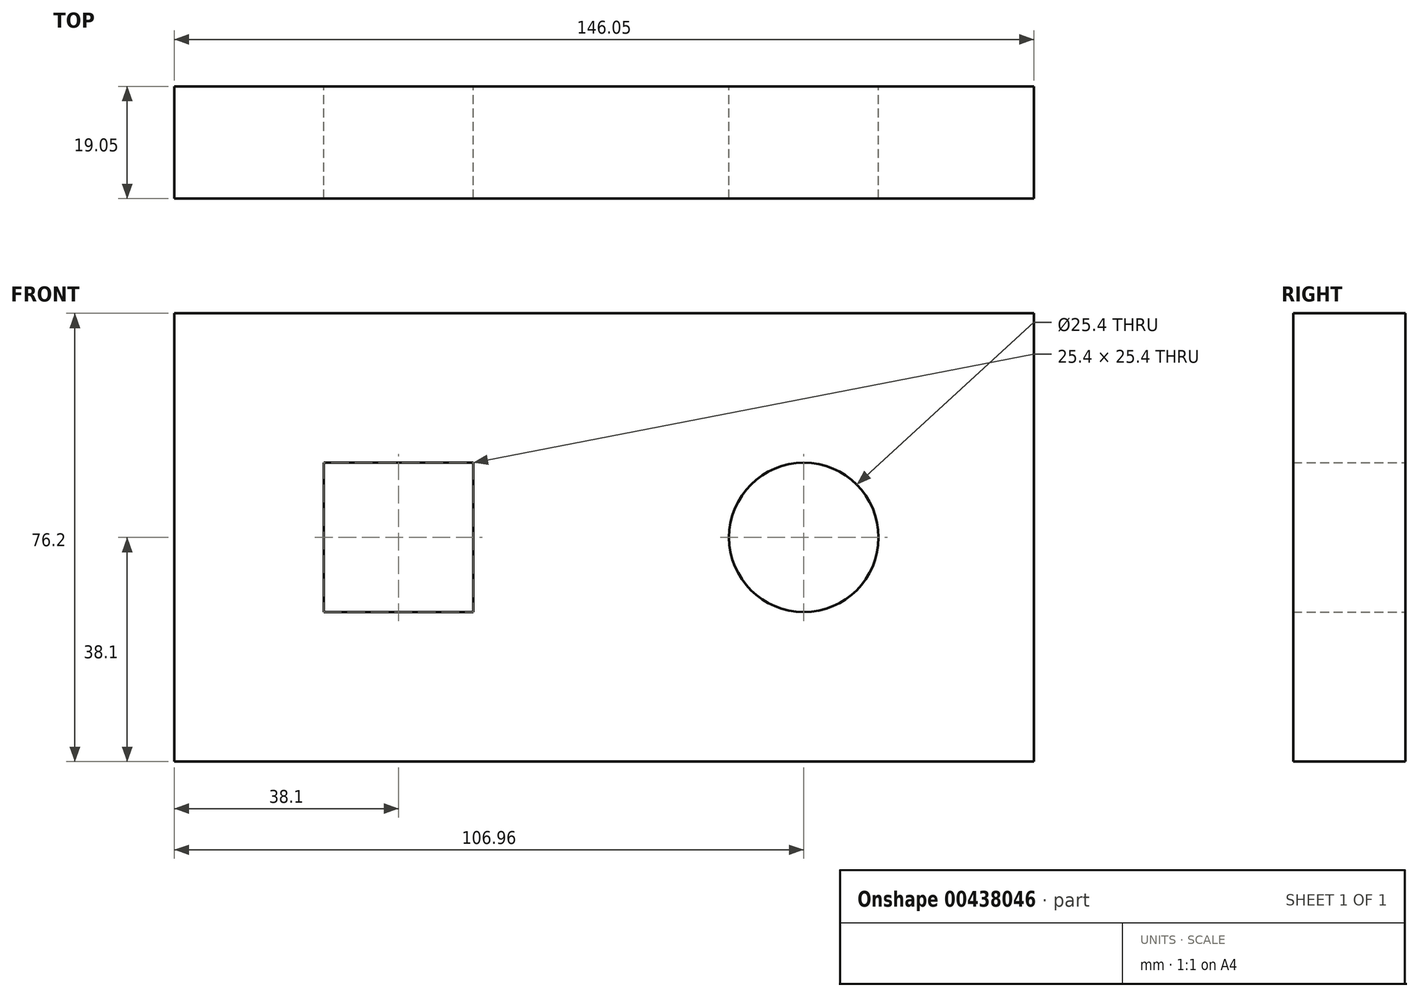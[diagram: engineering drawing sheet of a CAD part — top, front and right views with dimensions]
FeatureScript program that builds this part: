
annotation { "Feature Type Name" : "Feature", "Feature Type Description" : "" }
export const myFeature = defineFeature(function(context is Context, id is Id, definition is map)
    precondition{}
    {
        {
            var Q0;
            Q0=qCreatedBy(makeId("Front.planeOp"),FACE);
            var sketch = newSketch(context, id + "F0", { "sketchPlane" : qUnion([Q0])});
            skLineSegment(sketch, "E0", {"start": v(0, 0) * mm, "end": v(-146.05, 0) * mm});
            skLineSegment(sketch, "E1", {"start": v(-146.05, 0) * mm, "end": v(-146.05, 76.2) * mm});
            skLineSegment(sketch, "E2", {"start": v(-146.05, 76.2) * mm, "end": v(0, 76.2) * mm});
            skLineSegment(sketch, "E3", {"start": v(0, 76.2) * mm, "end": v(0, 0) * mm});
            skCircle(sketch, "E4", {"center": v(-39.1, 38.1) * mm, "radius": 12.7 * mm});
            skPoint(sketch, "E4.centerSnap0", {"position": v(0, 38.1) * mm});
            skLineSegment(sketch, "E5.bottom", {"start": v(-120.65, 50.8) * mm, "end": v(-95.25, 50.8) * mm});
            skLineSegment(sketch, "E5.top", {"start": v(-120.65, 25.4) * mm, "end": v(-95.25, 25.4) * mm});
            skLineSegment(sketch, "E5.left", {"start": v(-120.65, 50.8) * mm, "end": v(-120.65, 25.4) * mm});
            skLineSegment(sketch, "E5.right", {"start": v(-95.25, 50.8) * mm, "end": v(-95.25, 25.4) * mm});
            skSolve(sketch);
        }
        {
            var Q0;
            Q0=makeQuery(id+"F0.imprint","IMPRINT",FACE,{"disambiguationData":[TD([[makeQuery(id+"F0.imprint","IMPRINT",EDGE,{"derivedFrom":sQuery(id+"F0.wireOp",EDGE,"E0")}),-1.0]])]});
            extrude(context, id + "F1", {"entities" : qUnion([Q0]), "depth" : 19.05 * mm});
        }
    });
